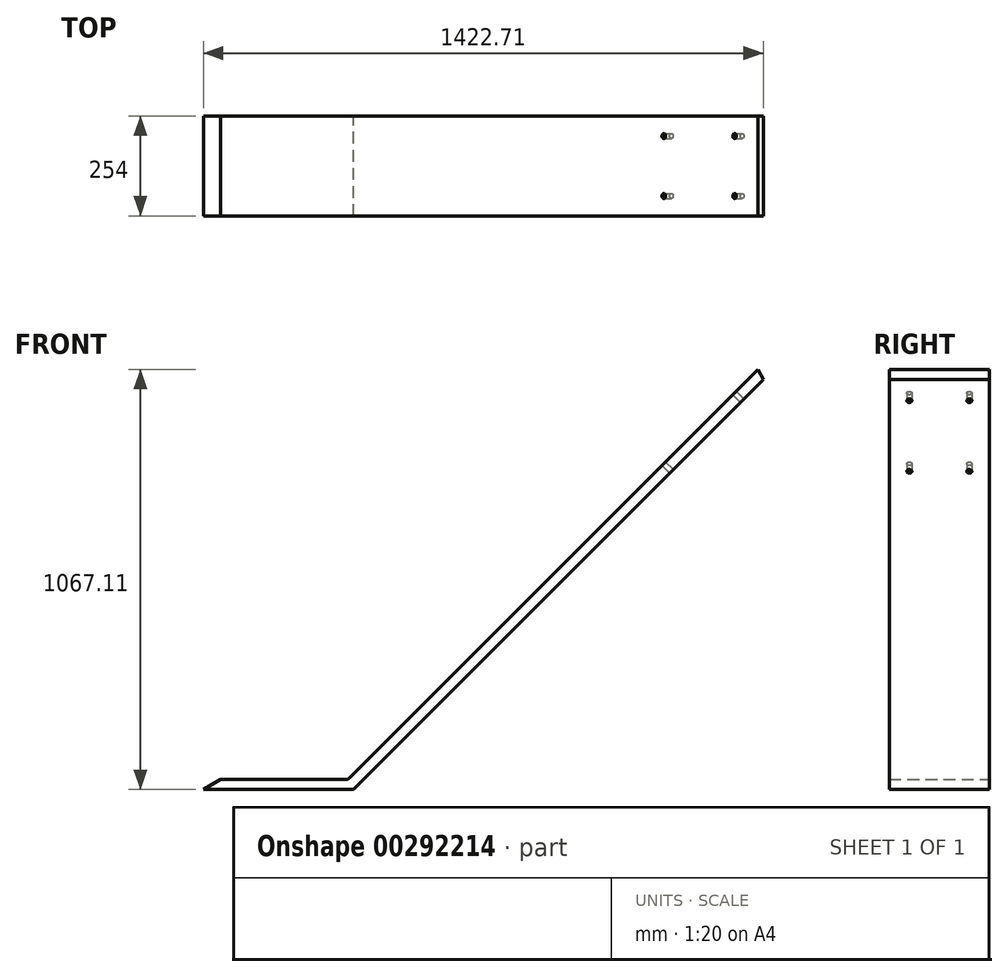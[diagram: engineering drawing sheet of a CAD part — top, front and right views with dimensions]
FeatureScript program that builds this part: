
annotation { "Feature Type Name" : "Feature", "Feature Type Description" : "" }
export const myFeature = defineFeature(function(context is Context, id is Id, definition is map)
    precondition{}
    {
        {
            var Q0;
            Q0=qCreatedBy(makeId("Front.planeOp"),FACE);
            var sketch = newSketch(context, id + "F0", { "sketchPlane" : qUnion([Q0])});
            skLineSegment(sketch, "E0", {"start": v(0, 0) * mm, "end": v(381, 0) * mm});
            skLineSegment(sketch, "E1", {"start": v(0, 0) * mm, "end": v(44, 25.4) * mm});
            skLineSegment(sketch, "E2", {"start": v(44, 25.4) * mm, "end": v(367.56, 25.4) * mm});
            skLineSegment(sketch, "E3", {"start": v(381, 0) * mm, "end": v(1422.7, 1041.7) * mm});
            skLineSegment(sketch, "E4", {"start": v(367.56, 25.4) * mm, "end": v(1409.27, 1067.1) * mm});
            skLineSegment(sketch, "E5", {"start": v(1409.27, 1067.1) * mm, "end": v(1422.7, 1041.7) * mm});
            skSolve(sketch);
        }
        {
            var Q0;
            Q0 = qSketchRegion(id + "F0", true);
            extrude(context, id + "F1", {"entities" : qUnion([Q0]), "depth" : 254 * mm});
        }
        {
            var Q0;
            Q0=makeQuery(id+"F1.opExtrude","SWEPT_EDGE",EDGE,{"disambiguationData":[OSD([sQuery(id+"F0.wireOp",EDGE,"E2"),sQuery(id+"F0.wireOp",EDGE,"E4")])]});
            fillet(context, id + "F2", {"entities" : qUnion([Q0]), "radius" : 12.7 * mm, "tangentPropagation" : true, "allowEdgeOverflow" : false});
        }
        {
            var Q0;
            Q0=makeQuery(id+"F1.opExtrude","SWEPT_FACE",FACE,{"disambiguationData":[OSD([sQuery(id+"F0.wireOp",EDGE,"E3")])]});
            var sketch = newSketch(context, id + "F3", { "sketchPlane" : qUnion([Q0])});
            skLineSegment(sketch, "E6", {"start": v(-127, 1742.6) * mm, "end": v(-127, 269.4) * mm, "construction": true});
            skPoint(sketch, "E7", {"position": v(-203.2, 1666.4) * mm});
            skPoint(sketch, "E8", {"position": v(-203.2, 1412.4) * mm});
            skPoint(sketch, "E9.MirrorP", {"position": v(-50.8, 1412.4) * mm});
            skPoint(sketch, "E10.MirrorP", {"position": v(-50.8, 1666.4) * mm});
            skSolve(sketch);
        }
        {
            var Q0;
            Q0=sQuery(id+"F3.wireOp",VERTEX,"E8");
            var Q1;
            Q1=sQuery(id+"F3.wireOp",VERTEX,"E7");
            var Q2;
            Q2=sQuery(id+"F3.wireOp",VERTEX,"E10.MirrorP");
            var Q3;
            Q3=sQuery(id+"F3.wireOp",VERTEX,"E9.MirrorP");
            var Q4;
            Q4=makeQuery(id+"F1.opExtrude","SWEPT_BODY",BODY,{"disambiguationData":[OSD([sQuery(id+"F0.wireOp",EDGE,"E0"),sQuery(id+"F0.wireOp",EDGE,"E1"),sQuery(id+"F0.wireOp",EDGE,"E2"),sQuery(id+"F0.wireOp",EDGE,"E3"),sQuery(id+"F0.wireOp",EDGE,"E4"),sQuery(id+"F0.wireOp",EDGE,"E5")])]});
            hole(context, id + "F4", {"style" : HoleStyle.SIMPLE, "endStyle" : HoleEndStyle.THROUGH, "holeDiameter" : 12.7 * mm, "tappedDepth" : 12.7 * mm, "tapClearance" : 3, "locations" : qUnion([Q0, Q1, Q2, Q3]), "scope" : qUnion([Q4])});
        }
    });
